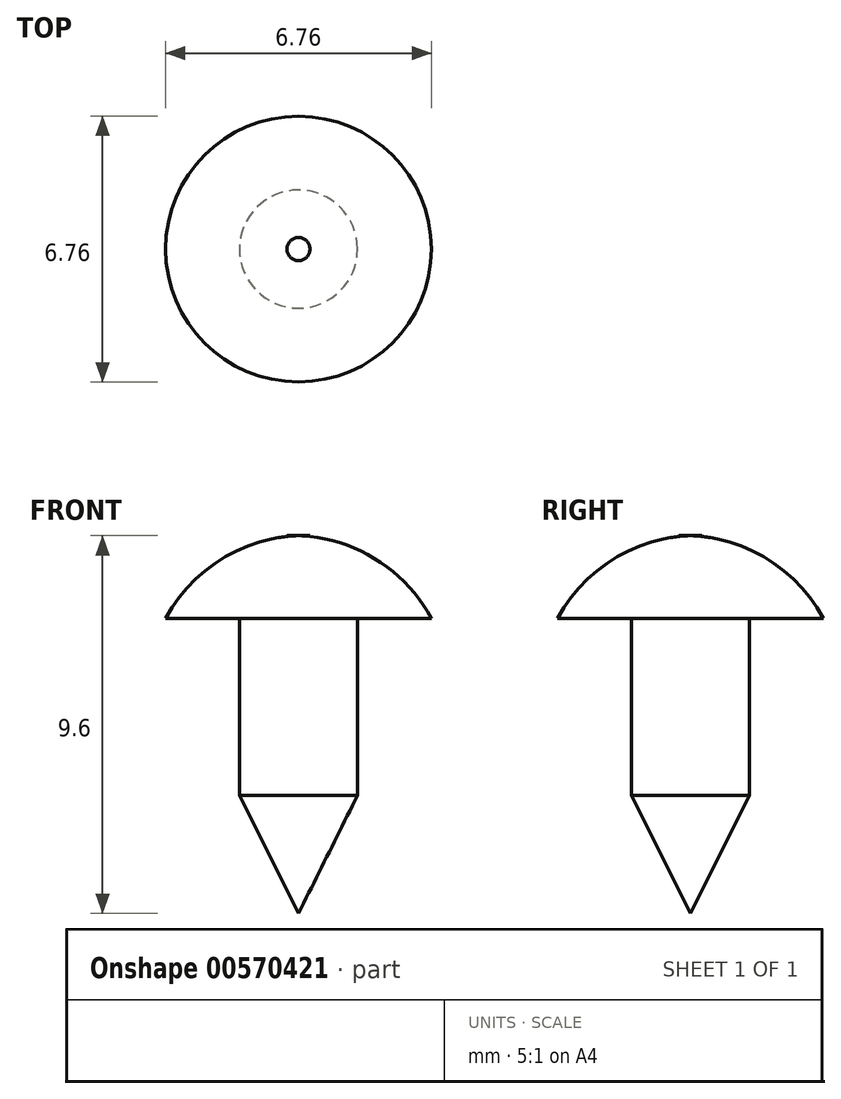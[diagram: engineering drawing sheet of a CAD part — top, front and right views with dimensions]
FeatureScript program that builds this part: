
annotation { "Feature Type Name" : "Feature", "Feature Type Description" : "" }
export const myFeature = defineFeature(function(context is Context, id is Id, definition is map)
    precondition{}
    {
        {
            var Q0;
            Q0=qCreatedBy(makeId("Top.planeOp"),FACE);
            var sketch = newSketch(context, id + "F0", { "sketchPlane" : qUnion([Q0])});
            skCircle(sketch, "E0", {"center": v(0, 0) * mm, "radius": 1.5 * mm});
            skSolve(sketch);
        }
        {
            var Q0;
            Q0=makeQuery(id+"F0.imprint","IMPRINT",FACE,{"disambiguationData":[TD([[makeQuery(id+"F0.imprint","IMPRINT",EDGE,{"derivedFrom":sQuery(id+"F0.wireOp",EDGE,"E0")}),1.0]])]});
            extrude(context, id + "F1", {"entities" : qUnion([Q0]), "depth" : 7.5 * mm, "offsetDistance" : 25 * mm});
        }
        {
            var Q0;
            Q0=qCreatedBy(makeId("Front.planeOp"),FACE);
            var sketch = newSketch(context, id + "F2", { "sketchPlane" : qUnion([Q0])});
            skLineSegment(sketch, "E1.0", {"start": v(-1.5, 7.5) * mm, "end": v(1.5, 7.5) * mm, "construction": true});
            skLineSegment(sketch, "E2", {"start": v(0, 7.5) * mm, "end": v(0, 9.6) * mm});
            skLineSegment(sketch, "E3", {"start": v(0, 7.5) * mm, "end": v(3.38, 7.5) * mm});
            skArc(sketch, "E4", {"start": v(3.38, 7.5) * mm, "mid": v(1.97, 9) * mm, "end": v(0, 9.6) * mm});
            skSolve(sketch);
        }
        {
            var Q0;
            Q0=makeQuery(id+"F2.imprint","IMPRINT",FACE,{"disambiguationData":[TD([[makeQuery(id+"F2.imprint","IMPRINT",EDGE,{"derivedFrom":sQuery(id+"F2.wireOp",EDGE,"E2")}),-1.0]])]});
            var Q1;
            Q1=sQuery(id+"F2.wireOp",EDGE,"E2");
            revolve(context, id + "F3", {"operationType" : NewBodyOperationType.ADD, "entities" : qUnion([Q0]), "axis" : qUnion([Q1]), "revolveType" : RevolveType.FULL});
        }
        {
            var Q0;
            Q0=makeQuery(id+"F1.opExtrude","CAP_EDGE",EDGE,{"disambiguationData":[OSD([sQuery(id+"F0.wireOp",EDGE,"E0")])],"isStart":true});
            chamfer(context, id + "F4", {"entities" : qUnion([Q0]), "chamferType" : ChamferType.TWO_OFFSETS, "width1" : 3 * mm, "oppositeDirection" : false, "width2" : 1.5 * mm, "tangentPropagation" : true});
        }
    });
